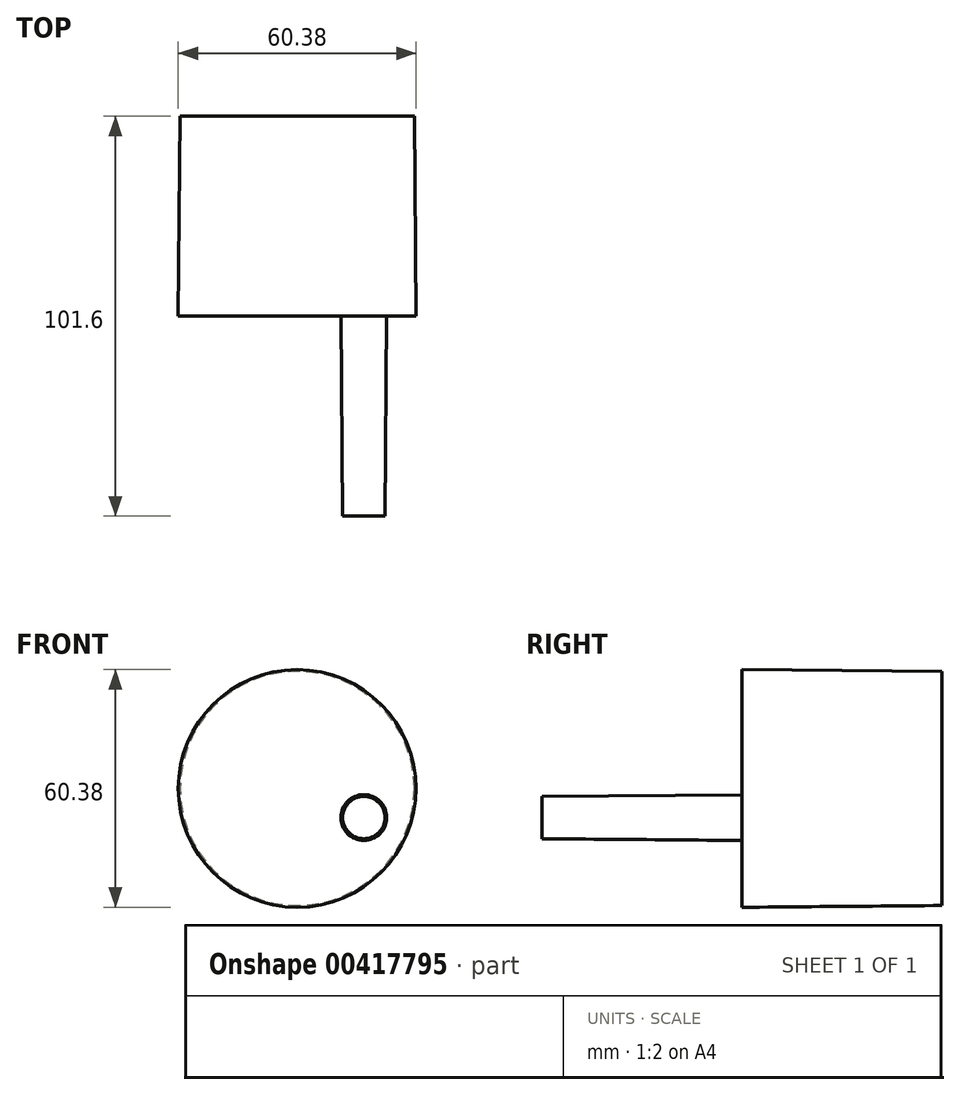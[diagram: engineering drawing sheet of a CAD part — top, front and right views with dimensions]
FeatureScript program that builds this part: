
annotation { "Feature Type Name" : "Feature", "Feature Type Description" : "" }
export const myFeature = defineFeature(function(context is Context, id is Id, definition is map)
    precondition{}
    {
        {
            var Q0;
            Q0=qCreatedBy(makeId("Front.planeOp"),FACE);
            var sketch = newSketch(context, id + "F0", { "sketchPlane" : qUnion([Q0])});
            skCircle(sketch, "E0", {"center": v(0, 0) * mm, "radius": 29.75 * mm});
            skSolve(sketch);
        }
        {
            var Q0;
            Q0 = qSketchRegion(id + "F0", true);
            extrude(context, id + "F1", {"entities" : qUnion([Q0]), "depth" : 50.8 * mm, "offsetDistance" : 25.4 * mm, "hasDraft" : true, "draftAngle" : 0.5 * degree});
        }
        {
            var Q0;
            Q0=makeQuery(id+"F1.opExtrude","CAP_FACE",FACE,{"disambiguationData":[OSD([sQuery(id+"F0.wireOp",EDGE,"E0")])],"isStart":false});
            var sketch = newSketch(context, id + "F2", { "sketchPlane" : qUnion([Q0])});
            skCircle(sketch, "E1", {"center": v(16.94, -7.4) * mm, "radius": 5.81 * mm});
            skSolve(sketch);
        }
        {
            var Q0;
            Q0 = qSketchRegion(id + "F2", true);
            extrude(context, id + "F3", {"entities" : qUnion([Q0]), "operationType" : NewBodyOperationType.ADD, "depth" : 50.8 * mm, "offsetDistance" : 25.4 * mm, "hasDraft" : true, "draftAngle" : 0.5 * degree, "draftPullDirection" : true});
        }
    });
